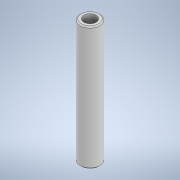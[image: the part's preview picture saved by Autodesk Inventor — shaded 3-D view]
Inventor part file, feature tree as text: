
AUTODESK INVENTOR PART (.ipt)
format: ipt  version: 2020 (Build 240168000, 168)  size: 103,424 bytes
history: native  units: mm
features: extrude x1, chamfer x1, sketch x1
ambient origin geometry x8: Origin, YZ Plane, XZ Plane, XY Plane, X Axis, Y Axis, Z Axis, Center Point
bodies: Solid1 (feature_tree)
feature tree (3):
  extrude  "Extrusion1"  Depth=50.0mm
  chamfer  "Chamfer1"  Distance=50.0mm
  sketch  "Sketch1"  dims[d0=8.0mm d1=5.0mm d2=50.0mm d3=0.0mm d4=0.5mm d5=2.0mm d6=45.0deg]
